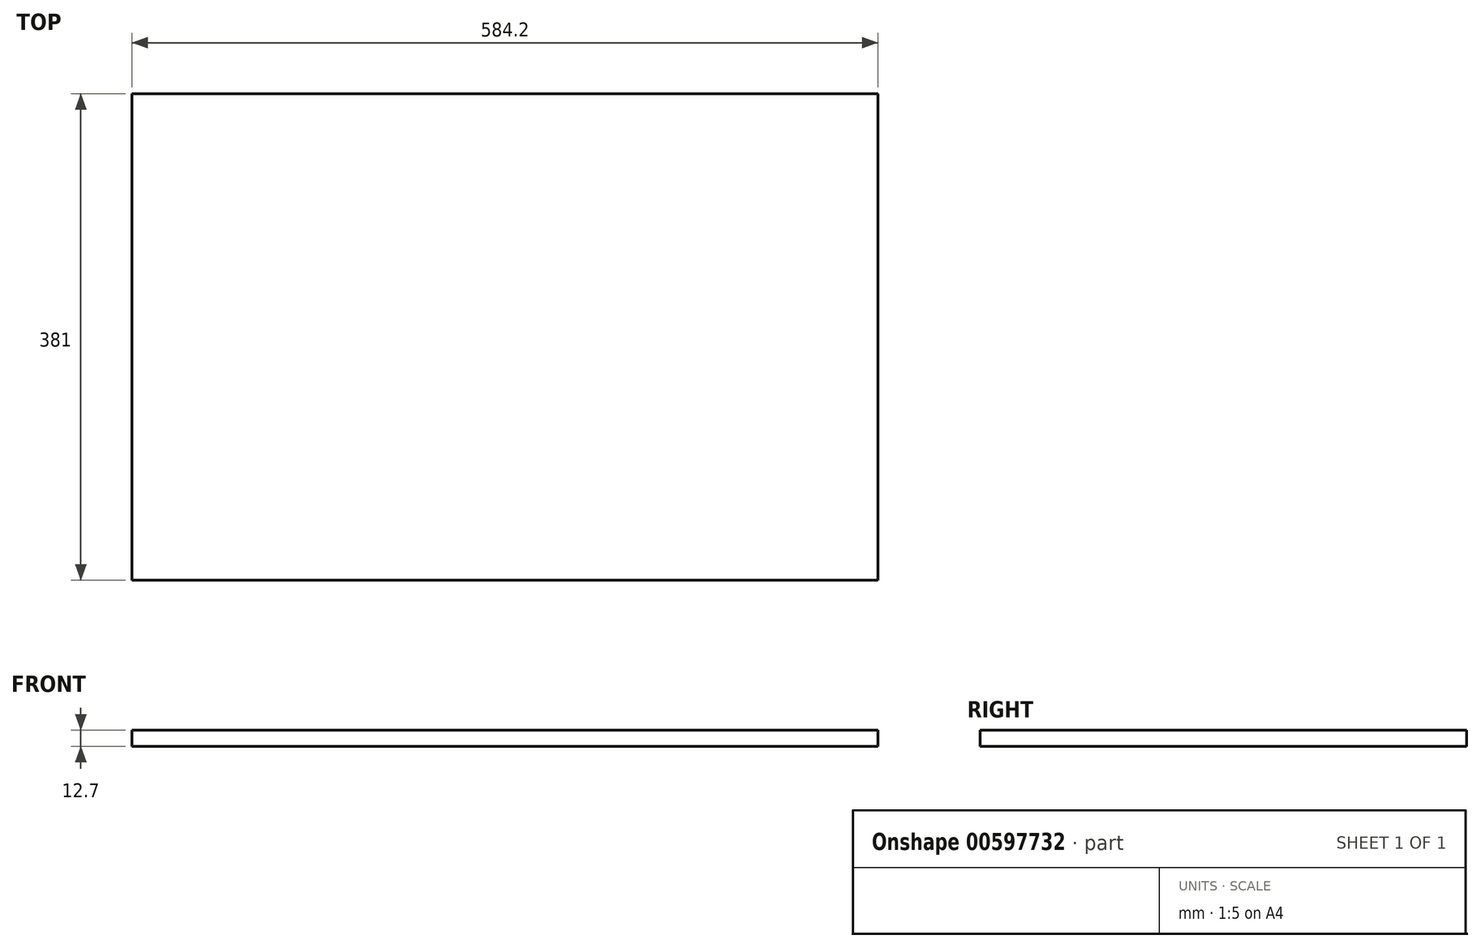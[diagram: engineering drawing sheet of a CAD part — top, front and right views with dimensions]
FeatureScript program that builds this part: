
annotation { "Feature Type Name" : "Feature", "Feature Type Description" : "" }
export const myFeature = defineFeature(function(context is Context, id is Id, definition is map)
    precondition{}
    {
        {
            var Q0;
            Q0=qCreatedBy(makeId("Top.planeOp"),FACE);
            var sketch = newSketch(context, id + "F0", { "sketchPlane" : qUnion([Q0])});
            skLineSegment(sketch, "E0.bottom", {"start": v(0, 381) * mm, "end": v(584.2, 381) * mm});
            skLineSegment(sketch, "E0.top", {"start": v(0, 0) * mm, "end": v(584.2, 0) * mm});
            skLineSegment(sketch, "E0.left", {"start": v(0, 381) * mm, "end": v(0, 0) * mm});
            skLineSegment(sketch, "E0.right", {"start": v(584.2, 381) * mm, "end": v(584.2, 0) * mm});
            skSolve(sketch);
        }
        {
            var Q0;
            Q0 = qSketchRegion(id + "F0", true);
            extrude(context, id + "F1", {"entities" : qUnion([Q0]), "depth" : 12.7 * mm, "offsetDistance" : 25.4 * mm});
        }
    });
